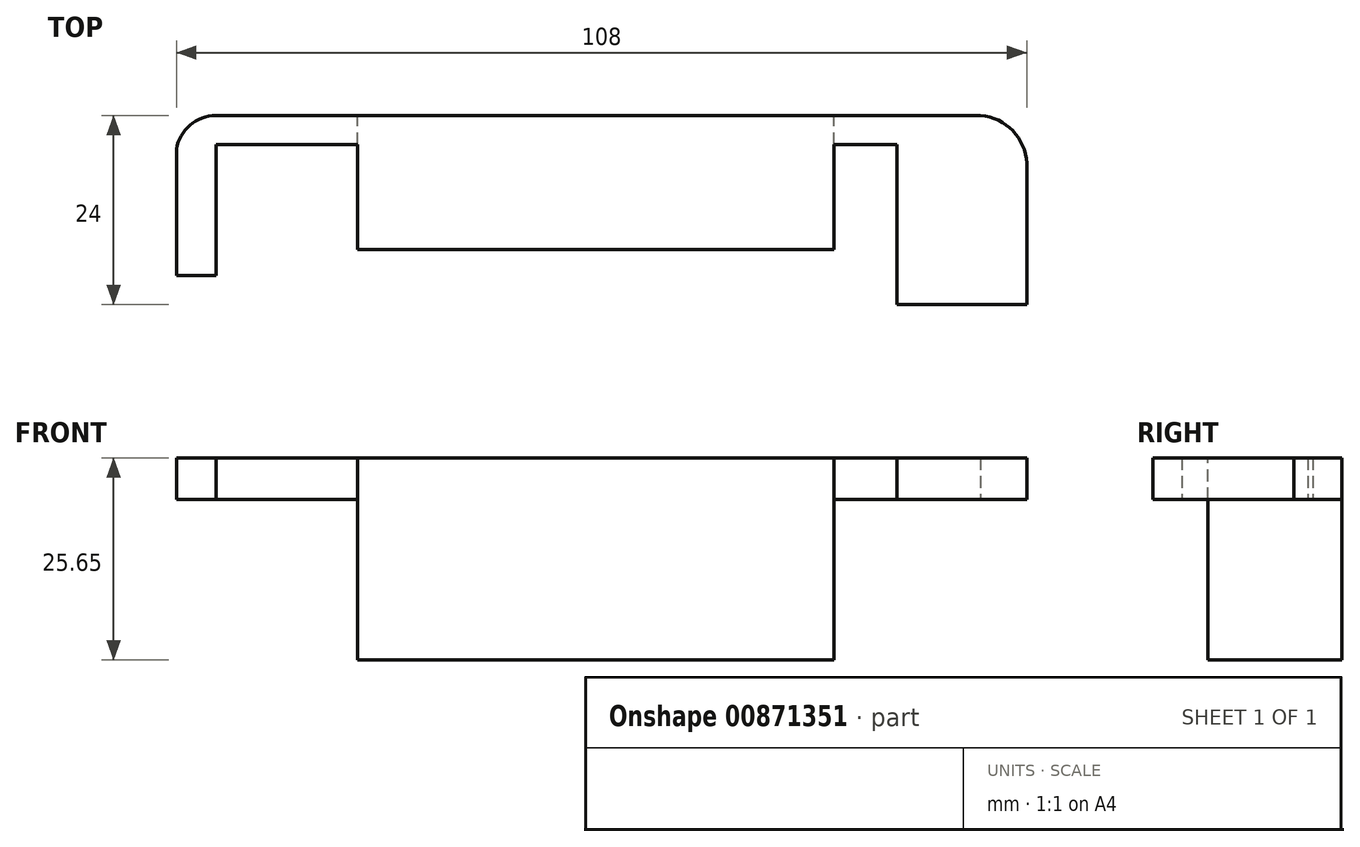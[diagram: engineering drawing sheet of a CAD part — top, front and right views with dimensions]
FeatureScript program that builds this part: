
annotation { "Feature Type Name" : "Feature", "Feature Type Description" : "" }
export const myFeature = defineFeature(function(context is Context, id is Id, definition is map)
    precondition{}
    {
        {
            var Q0;
            Q0=qCreatedBy(makeId("Top.planeOp"),FACE);
            var sketch = newSketch(context, id + "F0", { "sketchPlane" : qUnion([Q0])});
            skLineSegment(sketch, "E0.bottom", {"start": v(76.91, 12) * mm, "end": v(60.41, 12) * mm});
            skLineSegment(sketch, "E0.top", {"start": v(76.91, -12) * mm, "end": v(60.41, -12) * mm});
            skLineSegment(sketch, "E0.left", {"start": v(76.91, 12) * mm, "end": v(76.91, -12) * mm});
            skLineSegment(sketch, "E0.right", {"start": v(60.41, 12) * mm, "end": v(60.41, -12) * mm});
            skPoint(sketch, "E0.middle", {"position": v(68.66, 0) * mm});
            skLineSegment(sketch, "E1.bottom", {"start": v(-26.09, 12) * mm, "end": v(-31.09, 12) * mm});
            skLineSegment(sketch, "E1.top", {"start": v(-26.09, -8.32) * mm, "end": v(-31.09, -8.32) * mm});
            skLineSegment(sketch, "E1.left", {"start": v(-26.09, 12) * mm, "end": v(-26.09, -8.32) * mm});
            skLineSegment(sketch, "E1.right", {"start": v(-31.09, 12) * mm, "end": v(-31.09, -12) * mm});
            skPoint(sketch, "E1.middle", {"position": v(-28.59, 1.84) * mm});
            skArc(sketch, "E2", {"start": v(76.91, 5.36) * mm, "mid": v(74.98, 10.23) * mm, "end": v(70.05, 12) * mm});
            skArc(sketch, "E3", {"start": v(-26.09, 12) * mm, "mid": v(-29.38, 10.78) * mm, "end": v(-31.09, 7.72) * mm});
            skLineSegment(sketch, "E4.bottom", {"start": v(-26.09, 12) * mm, "end": v(60.41, 12) * mm});
            skLineSegment(sketch, "E4.top", {"start": v(-26.09, 8.35) * mm, "end": v(60.41, 8.35) * mm});
            skLineSegment(sketch, "E4.left", {"start": v(-26.09, 12) * mm, "end": v(-26.09, 8.35) * mm});
            skLineSegment(sketch, "E4.right", {"start": v(60.41, 12) * mm, "end": v(60.41, 8.35) * mm});
            skLineSegment(sketch, "E5.bottom", {"start": v(-8.09, 12) * mm, "end": v(52.41, 12) * mm});
            skLineSegment(sketch, "E5.top", {"start": v(-8.09, 18.85) * mm, "end": v(52.41, 18.85) * mm});
            skLineSegment(sketch, "E5.left", {"start": v(-8.09, 12) * mm, "end": v(-8.09, 18.85) * mm});
            skLineSegment(sketch, "E5.right", {"start": v(52.41, 12) * mm, "end": v(52.41, 18.85) * mm});
            skSolve(sketch);
        }
        {
            var Q0;
            {var subQ1=sQuery(id+"F0.wireOp",EDGE,"E0.top");Q0=makeQuery(id+"F0.imprint","IMPRINT",FACE,{"disambiguationData":[TD([[makeQuery(id+"F0.imprint","IMPRINT",EDGE,{"derivedFrom":subQ1}),-1.0]])]});}
            var Q1;
            {var subQ1=sQuery(id+"F0.wireOp",EDGE,"E1.top");Q1=makeQuery(id+"F0.imprint","IMPRINT",FACE,{"disambiguationData":[TD([[makeQuery(id+"F0.imprint","IMPRINT",EDGE,{"derivedFrom":subQ1}),-1.0]])]});}
            var Q2;
            {var subQ5=sQuery(id+"F0.wireOp",EDGE,"E4.top");Q2=makeQuery(id+"F0.imprint","IMPRINT",FACE,{"disambiguationData":[TD([[makeQuery(id+"F0.imprint","IMPRINT",EDGE,{"derivedFrom":subQ5}),1.0]])]});}
            var Q3;
            Q3=makeQuery(id+"F0.imprint","IMPRINT",FACE,{"disambiguationData":[TD([[makeQuery(id+"F0.imprint","IMPRINT",EDGE,{"derivedFrom":sQuery(id+"F0.wireOp",EDGE,"E5.top")}),-1.0]])]});
            extrude(context, id + "F1", {"entities" : qUnion([Q0, Q1, Q2, Q3]), "depth" : 5.25 * mm, "offsetDistance" : 25 * mm});
        }
        {
            var Q0;
            Q0=makeQuery(id+"F0.imprint","IMPRINT",FACE,{"disambiguationData":[TD([[makeQuery(id+"F0.imprint","IMPRINT",EDGE,{"derivedFrom":sQuery(id+"F0.wireOp",EDGE,"E5.top")}),-1.0]])]});
            extrude(context, id + "F2", {"entities" : qUnion([Q0]), "operationType" : NewBodyOperationType.ADD, "oppositeDirection" : true, "depth" : 20.4 * mm, "offsetDistance" : 25 * mm});
        }
        {
            var Q0;
            Q0=makeQuery(id+"F2.opExtrude","SWEPT_FACE",FACE,{"disambiguationData":[OSD([sQuery(id+"F0.wireOp",EDGE,"E4.bottom")])]});
            var sketch = newSketch(context, id + "F3", { "sketchPlane" : qUnion([Q0])});
            skLineSegment(sketch, "E6.bottom", {"start": v(-8.09, -20.4) * mm, "end": v(52.41, -20.4) * mm});
            skLineSegment(sketch, "E6.top", {"start": v(-8.09, 0) * mm, "end": v(52.41, 0) * mm});
            skLineSegment(sketch, "E6.left", {"start": v(-8.09, -20.4) * mm, "end": v(-8.09, 0) * mm});
            skLineSegment(sketch, "E6.right", {"start": v(52.41, -20.4) * mm, "end": v(52.41, 0) * mm});
            skSolve(sketch);
        }
        {
            var Q0;
            Q0 = qSketchRegion(id + "F3", true);
            extrude(context, id + "F4", {"entities" : qUnion([Q0]), "operationType" : NewBodyOperationType.ADD, "depth" : 3 * mm, "offsetDistance" : 25 * mm});
        }
        {
            var Q0;
            {var subQ0=sQuery(id+"F0.wireOp",EDGE,"E5.top");Q0=makeQuery(id+"F2.boolean.opBoolean","MERGE",FACE,{"derivedFrom":[makeQuery(id+"F1.opExtrude","SWEPT_FACE",FACE,{"disambiguationData":[OSD([subQ0])]}),makeQuery(id+"F2.opExtrude","SWEPT_FACE",FACE,{"disambiguationData":[OSD([subQ0])]})]});}
            extrude(context, id + "F5", {"entities" : qUnion([Q0]), "operationType" : NewBodyOperationType.ADD, "oppositeDirection" : true, "depth" : 7 * mm, "offsetDistance" : 25 * mm});
        }
        {
            var Q0;
            Q0=makeQuery(id+"F4.opExtrude","CAP_FACE",FACE,{"disambiguationData":[OSD([sQuery(id+"F3.wireOp",EDGE,"E6.bottom"),sQuery(id+"F3.wireOp",EDGE,"E6.top"),sQuery(id+"F3.wireOp",EDGE,"E6.left"),sQuery(id+"F3.wireOp",EDGE,"E6.right")])],"isStart":false});
            extrude(context, id + "F6", {"entities" : qUnion([Q0]), "operationType" : NewBodyOperationType.ADD, "depth" : 14 * mm, "offsetDistance" : 25 * mm});
        }
        {
            var Q0;
            {var subQ0=sQuery(id+"F0.wireOp",EDGE,"E5.top");Q0=makeQuery(id+"F2.boolean.opBoolean","MERGE",FACE,{"derivedFrom":[makeQuery(id+"F1.opExtrude","SWEPT_FACE",FACE,{"disambiguationData":[OSD([subQ0])]}),makeQuery(id+"F2.opExtrude","SWEPT_FACE",FACE,{"disambiguationData":[OSD([subQ0])]})]});}
            extrude(context, id + "F7", {"entities" : qUnion([Q0]), "operationType" : NewBodyOperationType.REMOVE, "oppositeDirection" : true, "depth" : 7.1 * mm, "offsetDistance" : 25 * mm});
        }
        {
            var Q0;
            Q0=makeQuery(id+"F6.opExtrude","SWEPT_FACE",FACE,{"disambiguationData":[OSD([sQuery(id+"F3.wireOp",EDGE,"E6.top")])]});
            extrude(context, id + "F8", {"entities" : qUnion([Q0]), "operationType" : NewBodyOperationType.ADD, "depth" : 5.25 * mm, "offsetDistance" : 25 * mm});
        }
        {
            var Q0;
            Q0=makeQuery(id+"F7.boolean.opBoolean","COPY",FACE,{"derivedFrom":makeQuery(id+"F7.opExtrude","CAP_FACE",FACE,{"disambiguationData":[OSD([sQuery(id+"F0.wireOp",EDGE,"E5.top")])],"isStart":false})});
            extrude(context, id + "F9", {"entities" : qUnion([Q0]), "operationType" : NewBodyOperationType.ADD, "depth" : 0.25 * mm, "offsetDistance" : 25 * mm});
        }
    });
